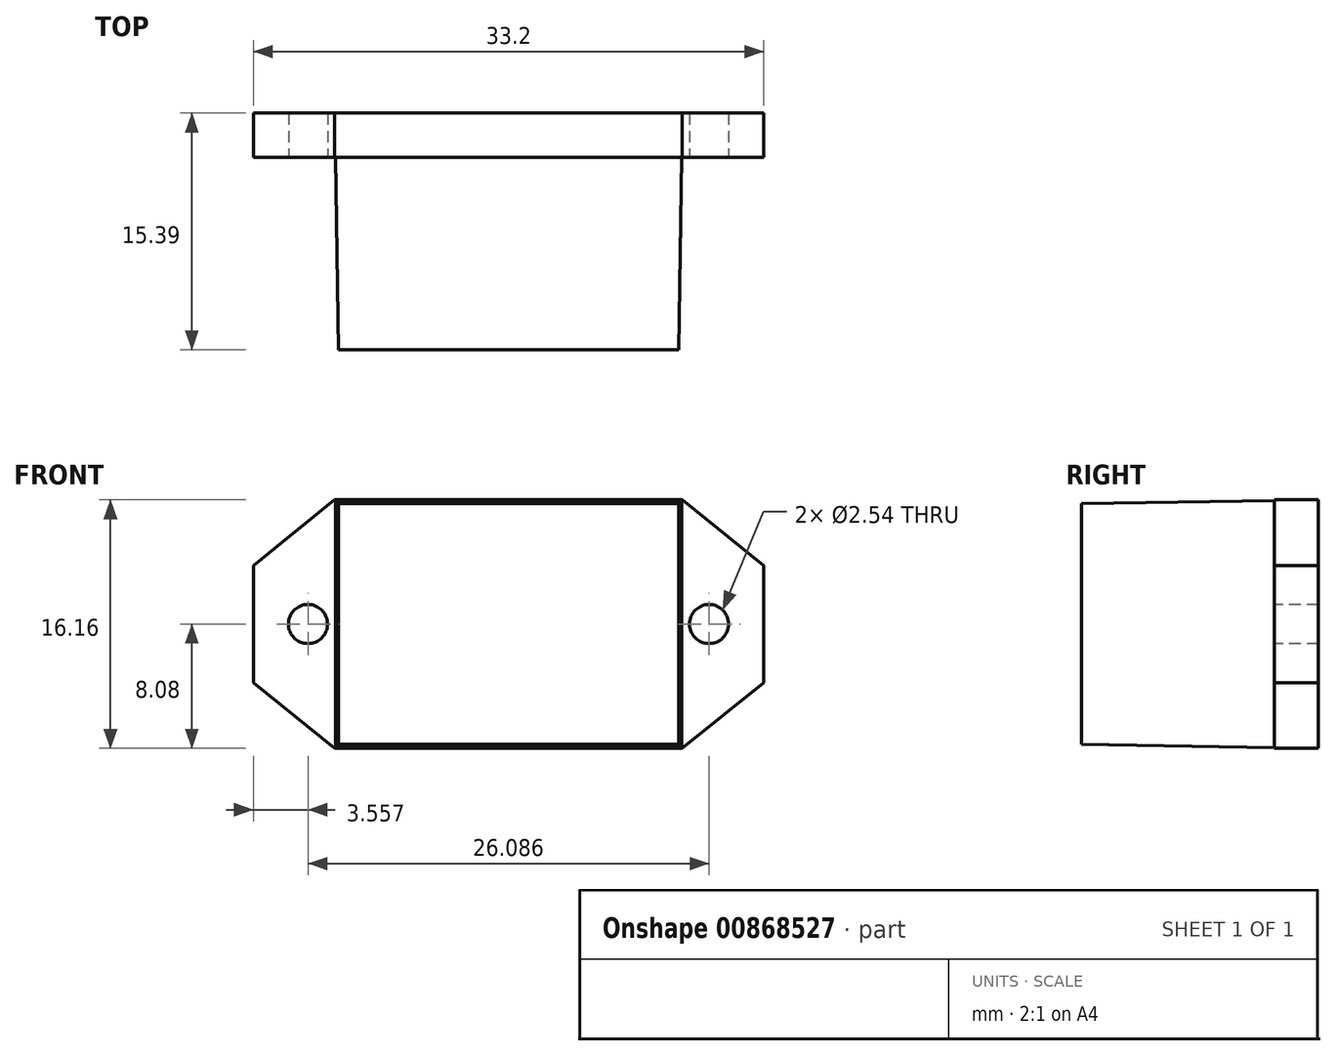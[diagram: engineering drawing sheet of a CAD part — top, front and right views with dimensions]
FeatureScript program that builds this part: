
annotation { "Feature Type Name" : "Feature", "Feature Type Description" : "" }
export const myFeature = defineFeature(function(context is Context, id is Id, definition is map)
    precondition{}
    {
        {
            var Q0;
            Q0=qCreatedBy(makeId("Front.planeOp"),FACE);
            var sketch = newSketch(context, id + "F0", { "sketchPlane" : qUnion([Q0])});
            skLineSegment(sketch, "E0.bottom", {"start": v(-11.3, 8.08) * mm, "end": v(11.3, 8.08) * mm});
            skLineSegment(sketch, "E0.top", {"start": v(-11.3, -8.08) * mm, "end": v(11.3, -8.08) * mm});
            skLineSegment(sketch, "E0.left", {"start": v(-11.3, 8.08) * mm, "end": v(-11.3, -8.08) * mm});
            skLineSegment(sketch, "E0.right", {"start": v(11.3, 8.08) * mm, "end": v(11.3, -8.08) * mm});
            skSolve(sketch);
        }
        {
            var Q0;
            Q0 = qSketchRegion(id + "F0", true);
            extrude(context, id + "F1", {"entities" : qUnion([Q0]), "depth" : 15.4 * mm, "offsetDistance" : 25.4 * mm, "hasDraft" : true, "draftAngle" : .9 * degree, "draftPullDirection" : true});
        }
        {
            var Q0;
            Q0=qCreatedBy(makeId("Front.planeOp"),FACE);
            var sketch = newSketch(context, id + "F2", { "sketchPlane" : qUnion([Q0])});
            skLineSegment(sketch, "E1", {"start": v(-16.6, 3.8) * mm, "end": v(-16.6, -3.81) * mm});
            skLineSegment(sketch, "E2", {"start": v(16.6, 3.81) * mm, "end": v(16.6, -3.8) * mm});
            skLineSegment(sketch, "E3", {"start": v(-16.6, 3.8) * mm, "end": v(-11.3, 8.08) * mm});
            skLineSegment(sketch, "E4", {"start": v(-11.3, 8.08) * mm, "end": v(11.3, 8.08) * mm});
            skLineSegment(sketch, "E5", {"start": v(11.3, 8.08) * mm, "end": v(16.6, 3.81) * mm});
            skLineSegment(sketch, "E6", {"start": v(16.6, -3.8) * mm, "end": v(11.3, -8.08) * mm});
            skLineSegment(sketch, "E7", {"start": v(11.3, -8.08) * mm, "end": v(-11.3, -8.08) * mm});
            skLineSegment(sketch, "E8", {"start": v(-11.3, -8.08) * mm, "end": v(-16.6, -3.81) * mm});
            skSolve(sketch);
        }
        {
            var Q0;
            Q0 = qSketchRegion(id + "F2", true);
            extrude(context, id + "F3", {"entities" : qUnion([Q0]), "operationType" : NewBodyOperationType.ADD, "depth" : 2.87 * mm, "offsetDistance" : 25.4 * mm});
        }
        {
            var Q0;
            {var subQ0=sQuery(id+"F2.wireOp",EDGE,"E2");var subQ1=sQuery(id+"F2.wireOp",EDGE,"E5");var subQ2=sQuery(id+"F2.wireOp",EDGE,"E6");Q0=makeQuery(id+"F3.boolean.opBoolean","SPLIT",FACE,{"disambiguationData":[TD([makeQuery(id+"F1.opExtrude","SWEPT_FACE",FACE,{"disambiguationData":[OSD([sQuery(id+"F0.wireOp",EDGE,"E0.right")])]})])],"derivedFrom":makeQuery(id+"F3.opExtrude","CAP_FACE",FACE,{"disambiguationData":[OSD([sQuery(id+"F2.wireOp",EDGE,"E1"),subQ0,sQuery(id+"F2.wireOp",EDGE,"E3"),sQuery(id+"F2.wireOp",EDGE,"E4"),subQ1,subQ2,sQuery(id+"F2.wireOp",EDGE,"E7"),sQuery(id+"F2.wireOp",EDGE,"E8")])],"isStart":false})});}
            var sketch = newSketch(context, id + "F4", { "sketchPlane" : qUnion([Q0])});
            skCircle(sketch, "E9", {"center": v(13.04, 0) * mm, "radius": 1.27 * mm});
            skCircle(sketch, "E10", {"center": v(-13.04, 0) * mm, "radius": 1.27 * mm});
            skSolve(sketch);
        }
        {
            var Q0;
            Q0 = qSketchRegion(id + "F4", true);
            extrude(context, id + "F5", {"entities" : qUnion([Q0]), "operationType" : NewBodyOperationType.REMOVE, "oppositeDirection" : true, "depth" : 25.4 * mm, "offsetDistance" : 25.4 * mm});
        }
    });
